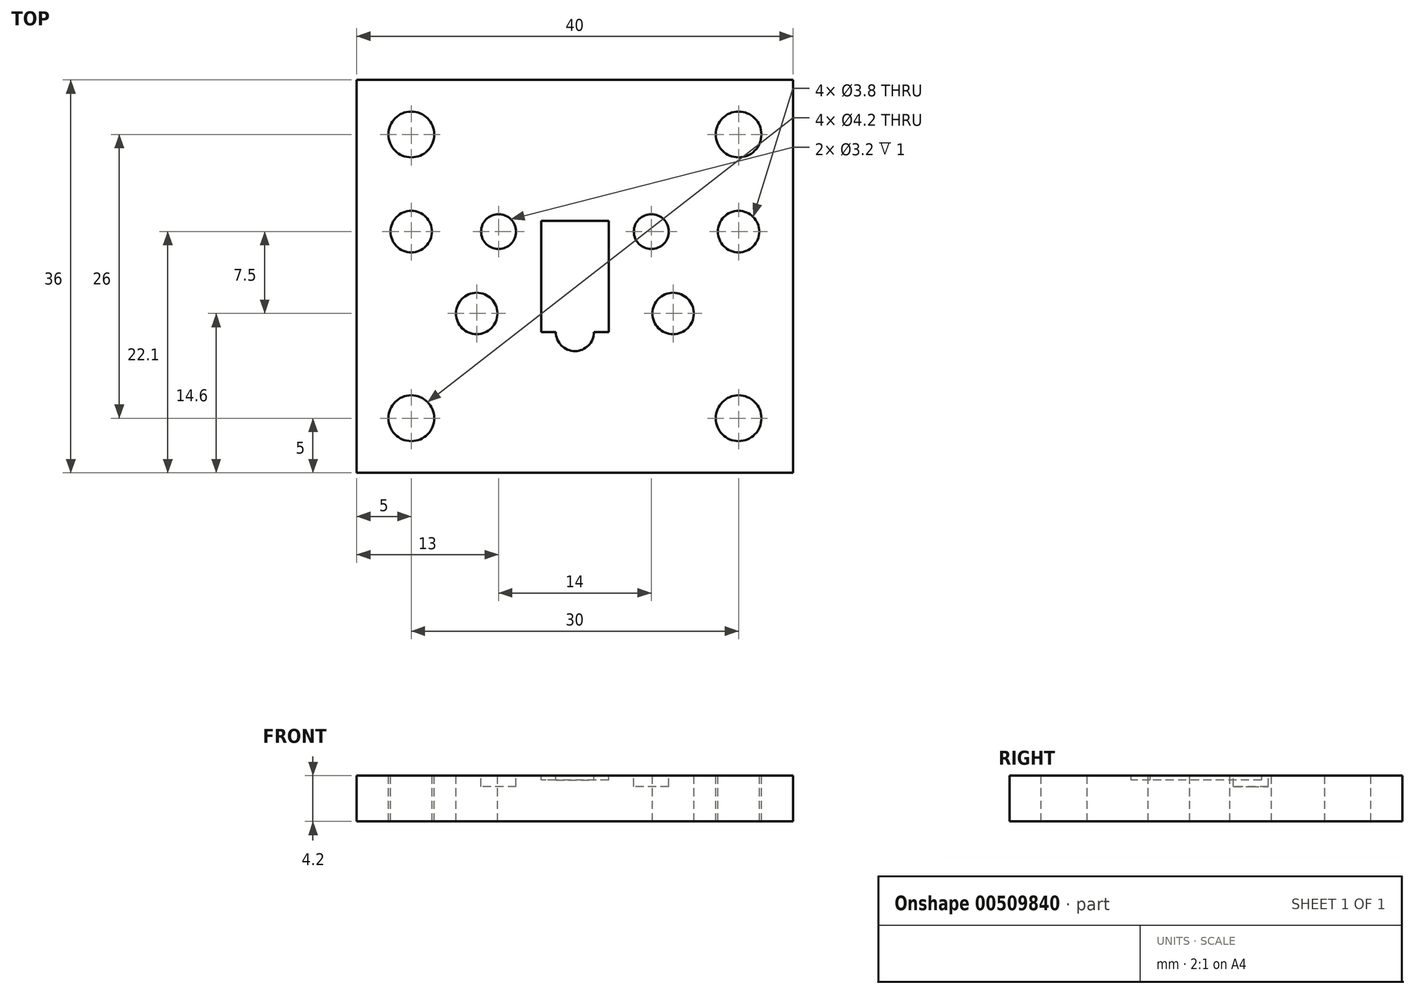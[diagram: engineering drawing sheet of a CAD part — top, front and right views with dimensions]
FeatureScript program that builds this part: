
annotation { "Feature Type Name" : "Feature", "Feature Type Description" : "" }
export const myFeature = defineFeature(function(context is Context, id is Id, definition is map)
    precondition{}
    {
        {
            var Q0;
            Q0=qCreatedBy(makeId("Top.planeOp"),FACE);
            var sketch = newSketch(context, id + "F0", { "sketchPlane" : qUnion([Q0])});
            skLineSegment(sketch, "E0.bottom", {"start": v(20, 18) * mm, "end": v(-20, 18) * mm});
            skLineSegment(sketch, "E0.top", {"start": v(20, -18) * mm, "end": v(-20, -18) * mm});
            skLineSegment(sketch, "E0.left", {"start": v(20, 18) * mm, "end": v(20, -18) * mm});
            skLineSegment(sketch, "E0.right", {"start": v(-20, 18) * mm, "end": v(-20, -18) * mm});
            skPoint(sketch, "E0.middle", {"position": v(0, 0) * mm});
            skSolve(sketch);
        }
        {
            var Q0;
            Q0 = qSketchRegion(id + "F0", true);
            extrude(context, id + "F1", {"entities" : qUnion([Q0]), "depth" : 4.2 * mm});
        }
        {
            var Q0;
            Q0=makeQuery(id+"F1.opExtrude","CAP_FACE",FACE,{"disambiguationData":[OSD([sQuery(id+"F0.wireOp",EDGE,"E0.bottom"),sQuery(id+"F0.wireOp",EDGE,"E0.top"),sQuery(id+"F0.wireOp",EDGE,"E0.left"),sQuery(id+"F0.wireOp",EDGE,"E0.right")])],"isStart":false});
            var sketch = newSketch(context, id + "F2", { "sketchPlane" : qUnion([Q0])});
            skLineSegment(sketch, "E1.bottom", {"start": v(3.1, 5.1) * mm, "end": v(-3.1, 5.1) * mm});
            skLineSegment(sketch, "E1.top", {"start": v(3.1, -5.1) * mm, "end": v(-3.1, -5.1) * mm});
            skLineSegment(sketch, "E1.left", {"start": v(3.1, 5.1) * mm, "end": v(3.1, -5.1) * mm});
            skLineSegment(sketch, "E1.right", {"start": v(-3.1, 5.1) * mm, "end": v(-3.1, -5.1) * mm});
            skPoint(sketch, "E1.middle", {"position": v(0, 0) * mm});
            skSolve(sketch);
        }
        {
            var Q0;
            Q0 = qSketchRegion(id + "F2", true);
            extrude(context, id + "F3", {"entities" : qUnion([Q0]), "operationType" : NewBodyOperationType.REMOVE, "oppositeDirection" : true, "depth" : 0.4 * mm, "offsetDistance" : 25 * mm});
        }
        {
            var Q0;
            Q0=makeQuery(id+"F1.opExtrude","CAP_FACE",FACE,{"disambiguationData":[OSD([sQuery(id+"F0.wireOp",EDGE,"E0.bottom"),sQuery(id+"F0.wireOp",EDGE,"E0.top"),sQuery(id+"F0.wireOp",EDGE,"E0.left"),sQuery(id+"F0.wireOp",EDGE,"E0.right")])],"isStart":false});
            var sketch = newSketch(context, id + "F4", { "sketchPlane" : qUnion([Q0])});
            skLineSegment(sketch, "E2", {"start": v(-17.87, 4.1) * mm, "end": v(18.62, 4.1) * mm});
            skCircle(sketch, "E3", {"center": v(-15, 4.1) * mm, "radius": 1.9 * mm});
            skCircle(sketch, "E4", {"center": v(15, 4.1) * mm, "radius": 1.9 * mm});
            skSolve(sketch);
        }
        {
            var Q0;
            Q0 = qSketchRegion(id + "F4", true);
            extrude(context, id + "F5", {"entities" : qUnion([Q0]), "operationType" : NewBodyOperationType.REMOVE, "oppositeDirection" : true, "depth" : 25 * mm});
        }
        {
            var Q0;
            Q0=makeQuery(id+"F1.opExtrude","CAP_FACE",FACE,{"disambiguationData":[OSD([sQuery(id+"F0.wireOp",EDGE,"E0.bottom"),sQuery(id+"F0.wireOp",EDGE,"E0.top"),sQuery(id+"F0.wireOp",EDGE,"E0.left"),sQuery(id+"F0.wireOp",EDGE,"E0.right")])],"isStart":false});
            var sketch = newSketch(context, id + "F6", { "sketchPlane" : qUnion([Q0])});
            skLineSegment(sketch, "E5", {"start": v(-8.75, 4.1) * mm, "end": v(8.25, 4.1) * mm});
            skCircle(sketch, "E6", {"center": v(-7, 4.1) * mm, "radius": 1.6 * mm});
            skCircle(sketch, "E7", {"center": v(7, 4.1) * mm, "radius": 1.6 * mm});
            skSolve(sketch);
        }
        {
            var Q0;
            Q0 = qSketchRegion(id + "F6", true);
            extrude(context, id + "F7", {"entities" : qUnion([Q0]), "operationType" : NewBodyOperationType.REMOVE, "oppositeDirection" : true, "depth" : 1 * mm, "offsetDistance" : 25 * mm});
        }
        {
            var Q0;
            Q0=makeQuery(id+"F1.opExtrude","CAP_FACE",FACE,{"disambiguationData":[OSD([sQuery(id+"F0.wireOp",EDGE,"E0.bottom"),sQuery(id+"F0.wireOp",EDGE,"E0.top"),sQuery(id+"F0.wireOp",EDGE,"E0.left"),sQuery(id+"F0.wireOp",EDGE,"E0.right")])],"isStart":false});
            var sketch = newSketch(context, id + "F8", { "sketchPlane" : qUnion([Q0])});
            skCircle(sketch, "E8", {"center": v(-9, -3.4) * mm, "radius": 1.9 * mm});
            skLineSegment(sketch, "E9", {"start": v(-15, 4.1) * mm, "end": v(15, 4.1) * mm});
            skCircle(sketch, "E10", {"center": v(9, -3.4) * mm, "radius": 1.9 * mm});
            skSolve(sketch);
        }
        {
            var Q0;
            Q0 = qSketchRegion(id + "F8", true);
            extrude(context, id + "F9", {"entities" : qUnion([Q0]), "operationType" : NewBodyOperationType.REMOVE, "endBound" : BoundingType.THROUGH_ALL, "oppositeDirection" : true, "depth" : 25 * mm, "offsetDistance" : 25 * mm});
        }
        {
            var Q0;
            Q0=makeQuery(id+"F1.opExtrude","CAP_FACE",FACE,{"disambiguationData":[OSD([sQuery(id+"F0.wireOp",EDGE,"E0.bottom"),sQuery(id+"F0.wireOp",EDGE,"E0.top"),sQuery(id+"F0.wireOp",EDGE,"E0.left"),sQuery(id+"F0.wireOp",EDGE,"E0.right")])],"isStart":false});
            var sketch = newSketch(context, id + "F10", { "sketchPlane" : qUnion([Q0])});
            skLineSegment(sketch, "E11.bottom", {"start": v(15, 13) * mm, "end": v(-15, 13) * mm});
            skLineSegment(sketch, "E11.top", {"start": v(15, -13) * mm, "end": v(-15, -13) * mm});
            skLineSegment(sketch, "E11.left", {"start": v(15, 13) * mm, "end": v(15, -13) * mm});
            skLineSegment(sketch, "E11.right", {"start": v(-15, 13) * mm, "end": v(-15, -13) * mm});
            skPoint(sketch, "E11.middle", {"position": v(0, 0) * mm});
            skCircle(sketch, "E12", {"center": v(-15, 13) * mm, "radius": 2.1 * mm});
            skCircle(sketch, "E13", {"center": v(15, 13) * mm, "radius": 2.1 * mm});
            skCircle(sketch, "E14", {"center": v(15, -13) * mm, "radius": 2.1 * mm});
            skCircle(sketch, "E15", {"center": v(-15, -13) * mm, "radius": 2.1 * mm});
            skSolve(sketch);
        }
        {
            var Q0;
            Q0=makeQuery(id+"F10.imprint","IMPRINT",FACE,{"disambiguationData":[TD([[makeQuery(id+"F10.imprint","IMPRINT",EDGE,{"derivedFrom":makeQuery(id+"F3.boolean.opBoolean","COPY",EDGE,{"derivedFrom":makeQuery(id+"F3.opExtrude","CAP_EDGE",EDGE,{"disambiguationData":[OSD([sQuery(id+"F2.wireOp",EDGE,"E1.bottom")])],"isStart":true})})}),1.0]])]});
            var Q1;
            Q1=makeQuery(id+"F10.imprint","IMPRINT",FACE,{"disambiguationData":[TD([[makeQuery(id+"F10.imprint","IMPRINT",EDGE,{"derivedFrom":makeQuery(id+"F7.boolean.opBoolean","COPY",EDGE,{"derivedFrom":makeQuery(id+"F7.opExtrude","CAP_EDGE",EDGE,{"disambiguationData":[OSD([sQuery(id+"F6.wireOp",EDGE,"E6")])],"isStart":true})})}),1.0]])]});
            var Q2;
            Q2=makeQuery(id+"F10.imprint","IMPRINT",FACE,{"disambiguationData":[TD([[makeQuery(id+"F10.imprint","IMPRINT",EDGE,{"derivedFrom":makeQuery(id+"F7.boolean.opBoolean","COPY",EDGE,{"derivedFrom":makeQuery(id+"F7.opExtrude","CAP_EDGE",EDGE,{"disambiguationData":[OSD([sQuery(id+"F6.wireOp",EDGE,"E7")])],"isStart":true})})}),1.0]])]});
            var Q3;
            Q3=makeQuery(id+"F10.imprint","IMPRINT",FACE,{"disambiguationData":[TD([[makeQuery(id+"F10.imprint","IMPRINT",EDGE,{"derivedFrom":makeQuery(id+"F9.boolean.opBoolean","COPY",EDGE,{"derivedFrom":makeQuery(id+"F9.opExtrude","CAP_EDGE",EDGE,{"disambiguationData":[OSD([sQuery(id+"F8.wireOp",EDGE,"E8")])],"isStart":true})})}),1.0]])]});
            var Q4;
            Q4=makeQuery(id+"F10.imprint","IMPRINT",FACE,{"disambiguationData":[TD([[makeQuery(id+"F10.imprint","IMPRINT",EDGE,{"derivedFrom":makeQuery(id+"F9.boolean.opBoolean","COPY",EDGE,{"derivedFrom":makeQuery(id+"F9.opExtrude","CAP_EDGE",EDGE,{"disambiguationData":[OSD([sQuery(id+"F8.wireOp",EDGE,"E10")])],"isStart":true})})}),1.0]])]});
            var Q5;
            {var subQ0=sQuery(id+"F10.wireOp",EDGE,"E11.left");var subQ1=sQuery(id+"F10.wireOp",EDGE,"E11.bottom");var subQ2=makeQuery(id+"F10.imprint","INTERSECT",VERTEX,{"derivedFrom":[subQ1,subQ0]});Q5=makeQuery(id+"F10.imprint","IMPRINT",FACE,{"disambiguationData":[TD([[makeQuery(id+"F10.imprint","IMPRINT",EDGE,{"disambiguationData":[TD([[subQ2,-1.0]])],"derivedFrom":subQ1}),1.0]])]});}
            var Q6;
            {var subQ0=sQuery(id+"F10.wireOp",EDGE,"E11.left");var subQ1=sQuery(id+"F10.wireOp",EDGE,"E11.bottom");var subQ2=makeQuery(id+"F10.imprint","INTERSECT",VERTEX,{"derivedFrom":[subQ1,subQ0]});Q6=makeQuery(id+"F10.imprint","IMPRINT",FACE,{"disambiguationData":[TD([[makeQuery(id+"F10.imprint","IMPRINT",EDGE,{"disambiguationData":[TD([[subQ2,-1.0]])],"derivedFrom":subQ1}),-1.0]])]});}
            var Q7;
            {var subQ0=sQuery(id+"F10.wireOp",EDGE,"E11.right");var subQ1=sQuery(id+"F10.wireOp",EDGE,"E11.bottom");var subQ2=makeQuery(id+"F10.imprint","INTERSECT",VERTEX,{"derivedFrom":[subQ1,subQ0]});Q7=makeQuery(id+"F10.imprint","IMPRINT",FACE,{"disambiguationData":[TD([[makeQuery(id+"F10.imprint","IMPRINT",EDGE,{"disambiguationData":[TD([[subQ2,1.0]])],"derivedFrom":subQ1}),-1.0]])]});}
            var Q8;
            {var subQ0=sQuery(id+"F10.wireOp",EDGE,"E11.right");var subQ1=sQuery(id+"F10.wireOp",EDGE,"E11.bottom");var subQ2=makeQuery(id+"F10.imprint","INTERSECT",VERTEX,{"derivedFrom":[subQ1,subQ0]});Q8=makeQuery(id+"F10.imprint","IMPRINT",FACE,{"disambiguationData":[TD([[makeQuery(id+"F10.imprint","IMPRINT",EDGE,{"disambiguationData":[TD([[subQ2,1.0]])],"derivedFrom":subQ1}),1.0]])]});}
            var Q9;
            {var subQ0=sQuery(id+"F10.wireOp",EDGE,"E11.left");var subQ1=sQuery(id+"F10.wireOp",EDGE,"E11.top");var subQ2=makeQuery(id+"F10.imprint","INTERSECT",VERTEX,{"derivedFrom":[subQ1,subQ0]});Q9=makeQuery(id+"F10.imprint","IMPRINT",FACE,{"disambiguationData":[TD([[makeQuery(id+"F10.imprint","IMPRINT",EDGE,{"disambiguationData":[TD([[subQ2,-1.0]])],"derivedFrom":subQ1}),-1.0]])]});}
            var Q10;
            {var subQ0=sQuery(id+"F10.wireOp",EDGE,"E11.left");var subQ1=sQuery(id+"F10.wireOp",EDGE,"E11.top");var subQ2=makeQuery(id+"F10.imprint","INTERSECT",VERTEX,{"derivedFrom":[subQ1,subQ0]});Q10=makeQuery(id+"F10.imprint","IMPRINT",FACE,{"disambiguationData":[TD([[makeQuery(id+"F10.imprint","IMPRINT",EDGE,{"disambiguationData":[TD([[subQ2,-1.0]])],"derivedFrom":subQ1}),1.0]])]});}
            var Q11;
            {var subQ0=sQuery(id+"F10.wireOp",EDGE,"E11.right");var subQ1=sQuery(id+"F10.wireOp",EDGE,"E11.top");var subQ2=makeQuery(id+"F10.imprint","INTERSECT",VERTEX,{"derivedFrom":[subQ1,subQ0]});Q11=makeQuery(id+"F10.imprint","IMPRINT",FACE,{"disambiguationData":[TD([[makeQuery(id+"F10.imprint","IMPRINT",EDGE,{"disambiguationData":[TD([[subQ2,1.0]])],"derivedFrom":subQ1}),-1.0]])]});}
            var Q12;
            {var subQ0=sQuery(id+"F10.wireOp",EDGE,"E11.right");var subQ1=sQuery(id+"F10.wireOp",EDGE,"E11.top");var subQ2=makeQuery(id+"F10.imprint","INTERSECT",VERTEX,{"derivedFrom":[subQ1,subQ0]});Q12=makeQuery(id+"F10.imprint","IMPRINT",FACE,{"disambiguationData":[TD([[makeQuery(id+"F10.imprint","IMPRINT",EDGE,{"disambiguationData":[TD([[subQ2,1.0]])],"derivedFrom":subQ1}),1.0]])]});}
            var Q13;
            {var subQ0=sQuery(id+"F10.wireOp",EDGE,"E11.left");var subQ1=makeQuery(id+"F5.boolean.opBoolean","COPY",EDGE,{"derivedFrom":makeQuery(id+"F5.opExtrude","CAP_EDGE",EDGE,{"disambiguationData":[OSD([sQuery(id+"F4.wireOp",EDGE,"E4")])],"isStart":true})});var subQ2=makeQuery(id+"F10.imprint","INTERSECT",VERTEX,{"disambiguationData":[OD(0.0)],"derivedFrom":[subQ1,subQ0]});Q13=makeQuery(id+"F10.imprint","IMPRINT",FACE,{"disambiguationData":[TD([[makeQuery(id+"F10.imprint","IMPRINT",EDGE,{"disambiguationData":[TD([[subQ2,-1.0]])],"derivedFrom":subQ0}),-1.0]])]});}
            var Q14;
            {var subQ0=sQuery(id+"F10.wireOp",EDGE,"E11.right");var subQ1=makeQuery(id+"F5.boolean.opBoolean","COPY",EDGE,{"derivedFrom":makeQuery(id+"F5.opExtrude","CAP_EDGE",EDGE,{"disambiguationData":[OSD([sQuery(id+"F4.wireOp",EDGE,"E3")])],"isStart":true})});var subQ2=makeQuery(id+"F10.imprint","INTERSECT",VERTEX,{"disambiguationData":[OD(0.0)],"derivedFrom":[subQ1,subQ0]});Q14=makeQuery(id+"F10.imprint","IMPRINT",FACE,{"disambiguationData":[TD([[makeQuery(id+"F10.imprint","IMPRINT",EDGE,{"disambiguationData":[TD([[subQ2,-1.0]])],"derivedFrom":subQ0}),1.0]])]});}
            extrude(context, id + "F11", {"entities" : qUnion([Q0, Q1, Q2, Q3, Q4, Q5, Q6, Q7, Q8, Q9, Q10, Q11, Q12, Q13, Q14]), "operationType" : NewBodyOperationType.REMOVE, "oppositeDirection" : true, "depth" : 25 * mm, "offsetDistance" : 25 * mm});
        }
        {
            var Q0;
            Q0=makeQuery(id+"F1.opExtrude","CAP_FACE",FACE,{"disambiguationData":[OSD([sQuery(id+"F0.wireOp",EDGE,"E0.bottom"),sQuery(id+"F0.wireOp",EDGE,"E0.top"),sQuery(id+"F0.wireOp",EDGE,"E0.left"),sQuery(id+"F0.wireOp",EDGE,"E0.right")])],"isStart":true});
            var sketch = newSketch(context, id + "F12", { "sketchPlane" : qUnion([Q0])});
            skLineSegment(sketch, "E16.bottom", {"start": v(3.1, 5.1) * mm, "end": v(-3.1, 5.1) * mm});
            skLineSegment(sketch, "E16.top", {"start": v(3.1, -5.1) * mm, "end": v(-3.1, -5.1) * mm});
            skLineSegment(sketch, "E16.left", {"start": v(3.1, 5.1) * mm, "end": v(3.1, -5.1) * mm});
            skLineSegment(sketch, "E16.right", {"start": v(-3.1, 5.1) * mm, "end": v(-3.1, -5.1) * mm});
            skPoint(sketch, "E16.middle", {"position": v(0, 0) * mm});
            skSolve(sketch);
        }
        {
            var Q0;
            Q0 = qSketchRegion(id + "F12", true);
            var Q1;
            Q1=makeQuery(id+"F1.opExtrude","CAP_FACE",FACE,{"disambiguationData":[OSD([sQuery(id+"F0.wireOp",EDGE,"E0.bottom"),sQuery(id+"F0.wireOp",EDGE,"E0.top"),sQuery(id+"F0.wireOp",EDGE,"E0.left"),sQuery(id+"F0.wireOp",EDGE,"E0.right")])],"isStart":false});
            extrude(context, id + "F13", {"entities" : qUnion([Q0]), "operationType" : NewBodyOperationType.ADD, "endBound" : BoundingType.UP_TO_SURFACE, "oppositeDirection" : true, "depth" : 25 * mm, "endBoundEntityFace" : qUnion([Q1]), "hasOffset" : true, "offsetDistance" : 0.4 * mm});
        }
        {
            var Q0;
            Q0=makeQuery(id+"F1.opExtrude","CAP_FACE",FACE,{"disambiguationData":[OSD([sQuery(id+"F0.wireOp",EDGE,"E0.bottom"),sQuery(id+"F0.wireOp",EDGE,"E0.top"),sQuery(id+"F0.wireOp",EDGE,"E0.left"),sQuery(id+"F0.wireOp",EDGE,"E0.right")])],"isStart":false});
            var sketch = newSketch(context, id + "F14", { "sketchPlane" : qUnion([Q0])});
            skArc(sketch, "E17", {"start": v(-1.75, -5.1) * mm, "mid": v(0, -6.85) * mm, "end": v(1.75, -5.1) * mm});
            skLineSegment(sketch, "E18", {"start": v(-1.75, -5.1) * mm, "end": v(1.75, -5.1) * mm});
            skSolve(sketch);
        }
        {
            var Q0;
            Q0 = qSketchRegion(id + "F14", true);
            extrude(context, id + "F15", {"entities" : qUnion([Q0]), "operationType" : NewBodyOperationType.REMOVE, "oppositeDirection" : true, "depth" : 0.4 * mm, "offsetDistance" : 25 * mm});
        }
        {
            var Q0;
            Q0=makeQuery(id+"F13.boolean.opBoolean","MERGE",FACE,{"derivedFrom":[makeQuery(id+"F1.opExtrude","CAP_FACE",FACE,{"disambiguationData":[OSD([sQuery(id+"F0.wireOp",EDGE,"E0.bottom"),sQuery(id+"F0.wireOp",EDGE,"E0.top"),sQuery(id+"F0.wireOp",EDGE,"E0.left"),sQuery(id+"F0.wireOp",EDGE,"E0.right")])],"isStart":true}),makeQuery(id+"F13.opExtrude","CAP_FACE",FACE,{"disambiguationData":[OSD([sQuery(id+"F12.wireOp",EDGE,"E16.bottom"),sQuery(id+"F12.wireOp",EDGE,"E16.top"),sQuery(id+"F12.wireOp",EDGE,"E16.left"),sQuery(id+"F12.wireOp",EDGE,"E16.right")])],"isStart":true})]});
            var sketch = newSketch(context, id + "F16", { "sketchPlane" : qUnion([Q0])});
            skCircle(sketch, "E19", {"center": v(7, -4.1) * mm, "radius": 1.6 * mm});
            skCircle(sketch, "E20", {"center": v(-7, -4.1) * mm, "radius": 1.6 * mm});
            skSolve(sketch);
        }
        {
            var Q0;
            Q0 = qSketchRegion(id + "F16", true);
            extrude(context, id + "F17", {"entities" : qUnion([Q0]), "operationType" : NewBodyOperationType.ADD, "oppositeDirection" : true, "depth" : 2 * mm, "offsetDistance" : 25 * mm});
        }
    });
